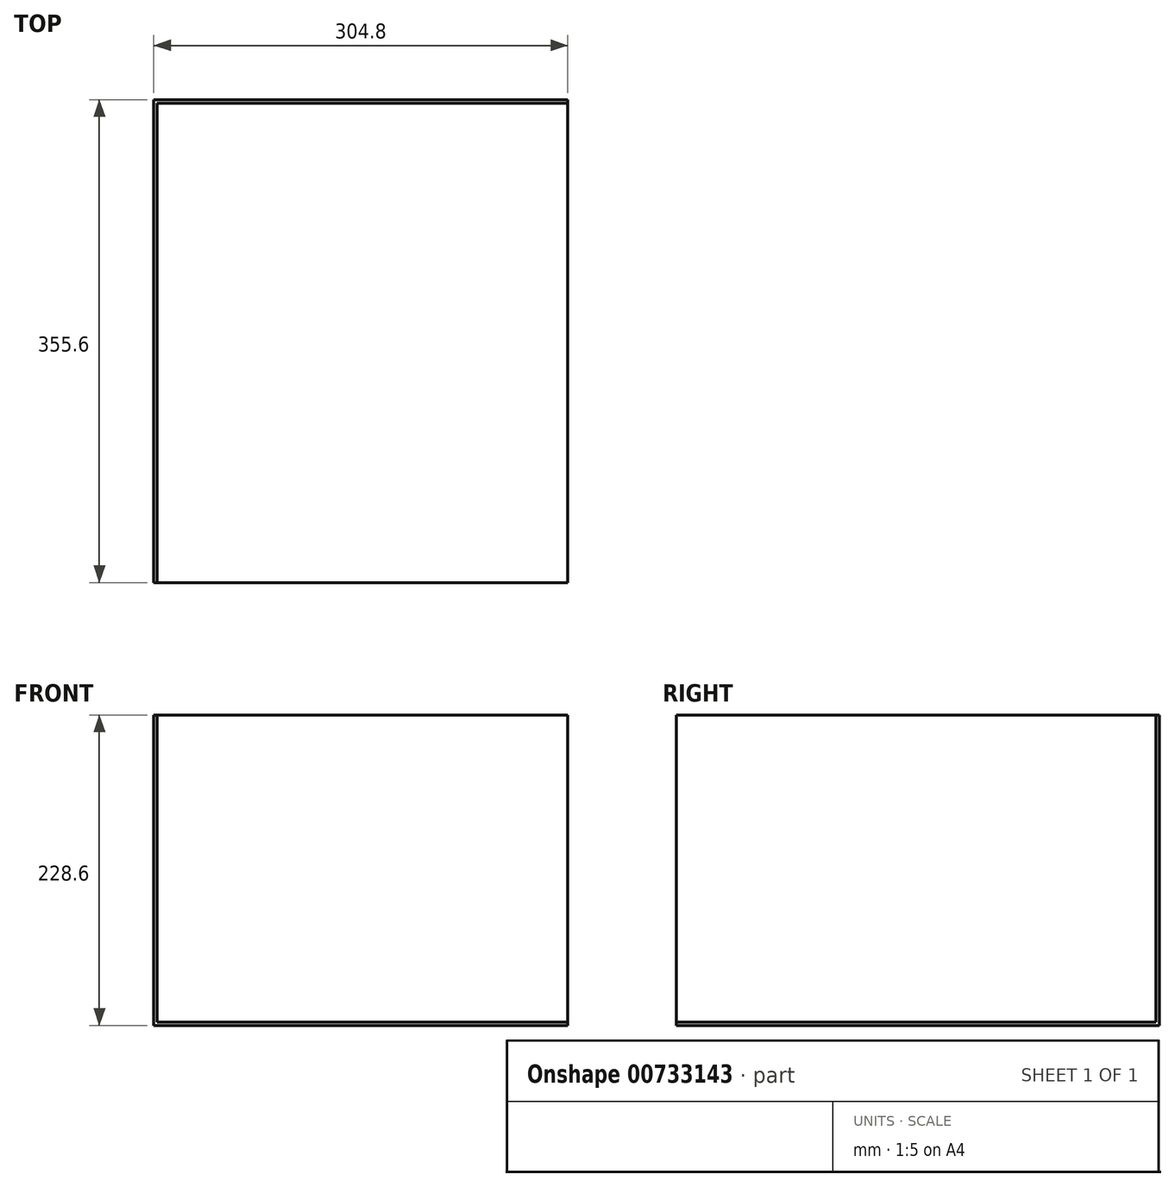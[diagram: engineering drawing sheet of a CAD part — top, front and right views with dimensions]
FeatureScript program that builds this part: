
annotation { "Feature Type Name" : "Feature", "Feature Type Description" : "" }
export const myFeature = defineFeature(function(context is Context, id is Id, definition is map)
    precondition{}
    {
        {
            var Q0;
            Q0=qCreatedBy(makeId("Top.planeOp"),FACE);
            var sketch = newSketch(context, id + "F0", { "sketchPlane" : qUnion([Q0])});
            skLineSegment(sketch, "E0.bottom", {"start": v(0, 0) * mm, "end": v(304.8, 0) * mm});
            skLineSegment(sketch, "E0.top", {"start": v(0, -355.6) * mm, "end": v(304.8, -355.6) * mm});
            skLineSegment(sketch, "E0.left", {"start": v(0, 0) * mm, "end": v(0, -355.6) * mm});
            skLineSegment(sketch, "E0.right", {"start": v(304.8, 0) * mm, "end": v(304.8, -355.6) * mm});
            skSolve(sketch);
        }
        {
            var Q0;
            Q0 = qSketchRegion(id + "F0", true);
            extrude(context, id + "F1", {"entities" : qUnion([Q0]), "depth" : 228.6 * mm, "offsetDistance" : 25.4 * mm});
        }
        {
            var Q0;
            Q0=makeQuery(id+"F1.opExtrude","CAP_FACE",FACE,{"disambiguationData":[OSD([sQuery(id+"F0.wireOp",EDGE,"E0.bottom"),sQuery(id+"F0.wireOp",EDGE,"E0.top"),sQuery(id+"F0.wireOp",EDGE,"E0.left"),sQuery(id+"F0.wireOp",EDGE,"E0.right")])],"isStart":false});
            var Q1;
            Q1=makeQuery(id+"F1.opExtrude","SWEPT_FACE",FACE,{"disambiguationData":[OSD([sQuery(id+"F0.wireOp",EDGE,"E0.top")])]});
            var Q2;
            Q2=makeQuery(id+"F1.opExtrude","SWEPT_FACE",FACE,{"disambiguationData":[OSD([sQuery(id+"F0.wireOp",EDGE,"E0.right")])]});
            shell(context, id + "F2", {"entities" : qUnion([Q0, Q1, Q2]), "thickness" : 2.54 * mm});
        }
    });
